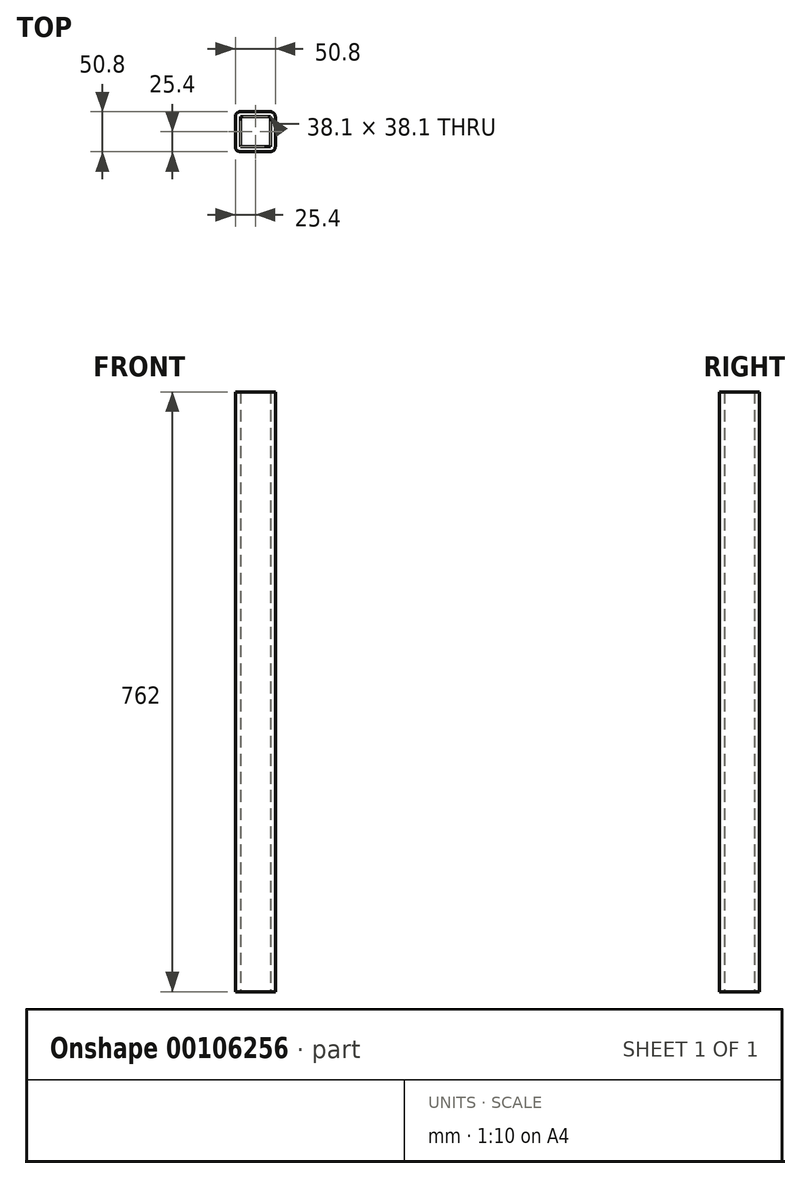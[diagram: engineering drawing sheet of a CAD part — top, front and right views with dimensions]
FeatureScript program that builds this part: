
annotation { "Feature Type Name" : "Feature", "Feature Type Description" : "" }
export const myFeature = defineFeature(function(context is Context, id is Id, definition is map)
    precondition{}
    {
        {
            var Q0;
            Q0=qCreatedBy(makeId("Top.planeOp"),FACE);
            var sketch = newSketch(context, id + "F0", { "sketchPlane" : qUnion([Q0])});
            skLineSegment(sketch, "E0.bottom", {"start": v(6.35, 0) * mm, "end": v(44.45, 0) * mm});
            skLineSegment(sketch, "E0.top", {"start": v(6.35, 50.8) * mm, "end": v(44.45, 50.8) * mm});
            skLineSegment(sketch, "E0.left", {"start": v(0, 6.35) * mm, "end": v(0, 44.45) * mm});
            skLineSegment(sketch, "E0.right", {"start": v(50.8, 6.35) * mm, "end": v(50.8, 44.45) * mm});
            skPoint(sketch, "E1.visualSharp", {"position": v(0, 50.8) * mm});
            skArc(sketch, "E1.filletArc", {"start": v(6.35, 50.8) * mm, "mid": v(1.86, 48.94) * mm, "end": v(0, 44.45) * mm});
            skPoint(sketch, "E2.visualSharp", {"position": v(50.8, 50.8) * mm});
            skArc(sketch, "E2.filletArc", {"start": v(50.8, 44.45) * mm, "mid": v(48.94, 48.94) * mm, "end": v(44.45, 50.8) * mm});
            skPoint(sketch, "E3.visualSharp", {"position": v(50.8, 0) * mm});
            skArc(sketch, "E3.filletArc", {"start": v(44.45, 0) * mm, "mid": v(48.94, 1.86) * mm, "end": v(50.8, 6.35) * mm});
            skPoint(sketch, "E4.visualSharp", {"position": v(0, 0) * mm});
            skArc(sketch, "E4.filletArc", {"start": v(0, 6.35) * mm, "mid": v(1.86, 1.86) * mm, "end": v(6.35, 0) * mm});
            skLineSegment(sketch, "E5.0", {"start": v(6.35, 6.35) * mm, "end": v(6.35, 44.45) * mm});
            skLineSegment(sketch, "E5.1", {"start": v(6.35, 6.35) * mm, "end": v(44.45, 6.35) * mm});
            skLineSegment(sketch, "E5.2", {"start": v(44.45, 6.35) * mm, "end": v(44.45, 44.45) * mm});
            skLineSegment(sketch, "E5.3", {"start": v(6.35, 44.45) * mm, "end": v(44.45, 44.45) * mm});
            skSolve(sketch);
        }
        {
            var Q0;
            Q0=makeQuery(id+"F0.imprint","IMPRINT",FACE,{"disambiguationData":[TD([[makeQuery(id+"F0.imprint","IMPRINT",EDGE,{"derivedFrom":sQuery(id+"F0.wireOp",EDGE,"E0.bottom")}),1.0]])]});
            extrude(context, id + "F1", {"entities" : qUnion([Q0]), "depth" : 762 * mm});
        }
    });
